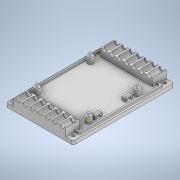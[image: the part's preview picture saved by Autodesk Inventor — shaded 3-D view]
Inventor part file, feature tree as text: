
AUTODESK INVENTOR PART (.ipt)
format: ipt  version: 2021 (Build 250183000, 183)  size: 600,064 bytes
history: native  units: mm
features: extrude x19, sketch x19, fillet x6
ambient origin geometry x8: Origin, YZ Plane, XZ Plane, XY Plane, X Axis, Y Axis, Z Axis, Center Point
bodies: Solid1 (feature_tree)
feature tree (44):
  extrude  "Extrusion1"  Depth=62.0mm
  extrude  "Extrusion2"  Depth=3.0mm
  extrude  "Extrusion3"  Depth=3.0mm
  extrude  "Extrusion4"  Depth=3.0mm
  fillet  "Fillet1"  Radius=6.0mm
  fillet  "Fillet2"  Radius=3.0mm
  fillet  "Fillet3"  Radius=57.4mm
  extrude  "Extrusion7"  Depth=0.8mm
  extrude  "Extrusion8"  Depth=4.8mm
  extrude  "Extrusion9"  Depth=6.0mm
  extrude  "Extrusion10"  Depth=20.0mm
  extrude  "Extrusion11"  Depth=1.0mm
  extrude  "Extrusion12"  Depth=2.0mm TaperAngle=0.0deg
  extrude  "Extrusion13"  TaperAngle=0.0deg  [1 undecoded]
  fillet  "Fillet8"  [1 undecoded]
  fillet  "Fillet9"  Radius=6.0mm
  extrude  "Extrusion14"  TaperAngle=0.0deg  [1 undecoded]
  extrude  "Extrusion15"  Depth=2.0mm
  extrude  "Extrusion16"  Depth=4.0mm
  extrude  "Extrusion17"  Depth=4.0mm
  fillet  "Fillet11"  Radius=2.0mm
  extrude  "Extrusion18"  Depth=2.0mm
  extrude  "Extrusion19"  Depth=35.0mm
  sketch  "Sketch25"  dims[d75=2.0mm d76=35.0mm]
  extrude  "Extrusion20"  Depth=4.0mm TaperAngle=0.0deg
  extrude  "Extrusion21"  Depth=1.0mm
  sketch  "Sketch2"  dims[d14=66.0mm d15=62.0mm]
  sketch  "Sketch4"  dims[d16=3.0mm d17=3.0mm]
  sketch  "Sketch5"  dims[d18=3.0mm d19=3.0mm]
  sketch  "Sketch6"  dims[d20=3.0mm d21=4.5mm d22=6.0mm d23=3.0mm d24=57.4mm]
  sketch  "Sketch10"  dims[d25=54.35mm d26=0.8mm]
  sketch  "Sketch11"  dims[d27=51.56mm d28=4.8mm]
  sketch  "Sketch12"  dims[d29=6.0mm d30=6.0mm]
  sketch  "Sketch13"  dims[d31=6.0mm d32=20.0mm]
  sketch  "Sketch14"  dims[d33=20.0mm d34=1.0mm]
  sketch  "Sketch17"  dims[d35=1.0mm d36=2.0mm d37=0.0mm]
  sketch  "Sketch19"  dims[d38=66.0mm d39=62.0mm d40=3.0mm d41=3.0mm d42=3.0mm d43=3.0mm d44=3.0mm d45=4.5mm d46=6.0mm d47=3.0mm d48=57.4mm d49=54.35mm d50=0.8mm d51=51.56mm d52=4.8mm d53=6.0mm d54=6.0mm d55=6.0mm d56=20.0mm d57=20.0mm d58=1.0mm d59=1.0mm d60=0.0mm d61=0.0mm d62=6.0mm d63=0.0mm]
  sketch  "Sketch20"  dims[d64=2.0mm d65=0.0mm]
  sketch  "Sketch21"  dims[d66=2.0mm d67=2.0mm]
  sketch  "Sketch22"  dims[d68=30.0mm d69=4.0mm]
  sketch  "Sketch23"  dims[d70=4.0mm d71=4.0mm d72=2.0mm]
  sketch  "Sketch24"  dims[d73=2.0mm d74=2.0mm]
  sketch  "Sketch26"  dims[d77=8.0mm d78=0.0mm d79=4.0mm d80=0.0mm]
  sketch  "Sketch27"  dims[d81=1.0mm d82=1.0mm d83=1.0mm d122=15.0mm d123=15.0mm d124=56.0mm d125=4.0mm d126=12.0mm d127=56.0mm d128=4.0mm d129=12.0mm d130=8.0mm d131=0.0mm d132=6.0mm d133=4.0mm d134=70.0mm d136=8.0mm d137=10.0mm d139=10.0mm d141=11.0mm d142=0.0mm d143=6.2mm d144=4.0mm d145=70.0mm d147=8.0mm d148=10.0mm d150=10.0mm d152=11.0mm d153=0.0mm d158=1.0mm d159=1.0mm d160=8.0mm d161=2.0mm d162=0.0mm d163=0.0mm d164=0.0mm d165=4.0mm d166=4.0mm d167=0.0mm d168=2.0mm d169=0.0mm d177=2.0mm d178=2.0mm d179=8.0mm d180=0.0mm d181=2.0mm d182=2.0mm d184=2.0mm d186=2.0mm d187=8.0mm d190=8.0mm d193=8.0mm d196=8.0mm d199=2.0mm d200=2.0mm d201=2.0mm d202=2.0mm d203=2.0mm d204=0.0mm d205=0.5mm d206=0.5mm d211=10.0mm d212=0.0mm d213=2.0mm d214=0.0mm d215=8.0mm d216=5.0mm d217=5.0mm d218=3.0mm d219=8.0mm d220=8.0mm d221=8.0mm d222=5.0mm d223=5.0mm d224=5.0mm d225=5.0mm d226=3.0mm d227=3.0mm d228=3.0mm d229=10.0mm d230=0.0mm d231=7.0mm d232=7.0mm d233=7.0mm d234=7.0mm d235=2.0mm d236=0.0mm d237=2.0mm d238=4.5mm d239=4.0mm d240=70.0mm d242=8.0mm d243=10.0mm d245=10.0mm d247=20.0mm d248=0.0mm d249=4.0mm d250=4.5mm d251=70.0mm d253=8.0mm d254=10.0mm d256=10.0mm d258=20.0mm d259=0.0mm d260=5.0mm d261=5.0mm d262=6.0mm d263=0.0mm d264=2.5mm d265=2.5mm d266=2.5mm d267=2.5mm d268=3.0mm d269=0.0mm]
note: 3 required parameter values undecoded (feature->parameter linkage not recoverable at this tier; creation-order binding heuristic only, values carry confidence <= 0.55)
